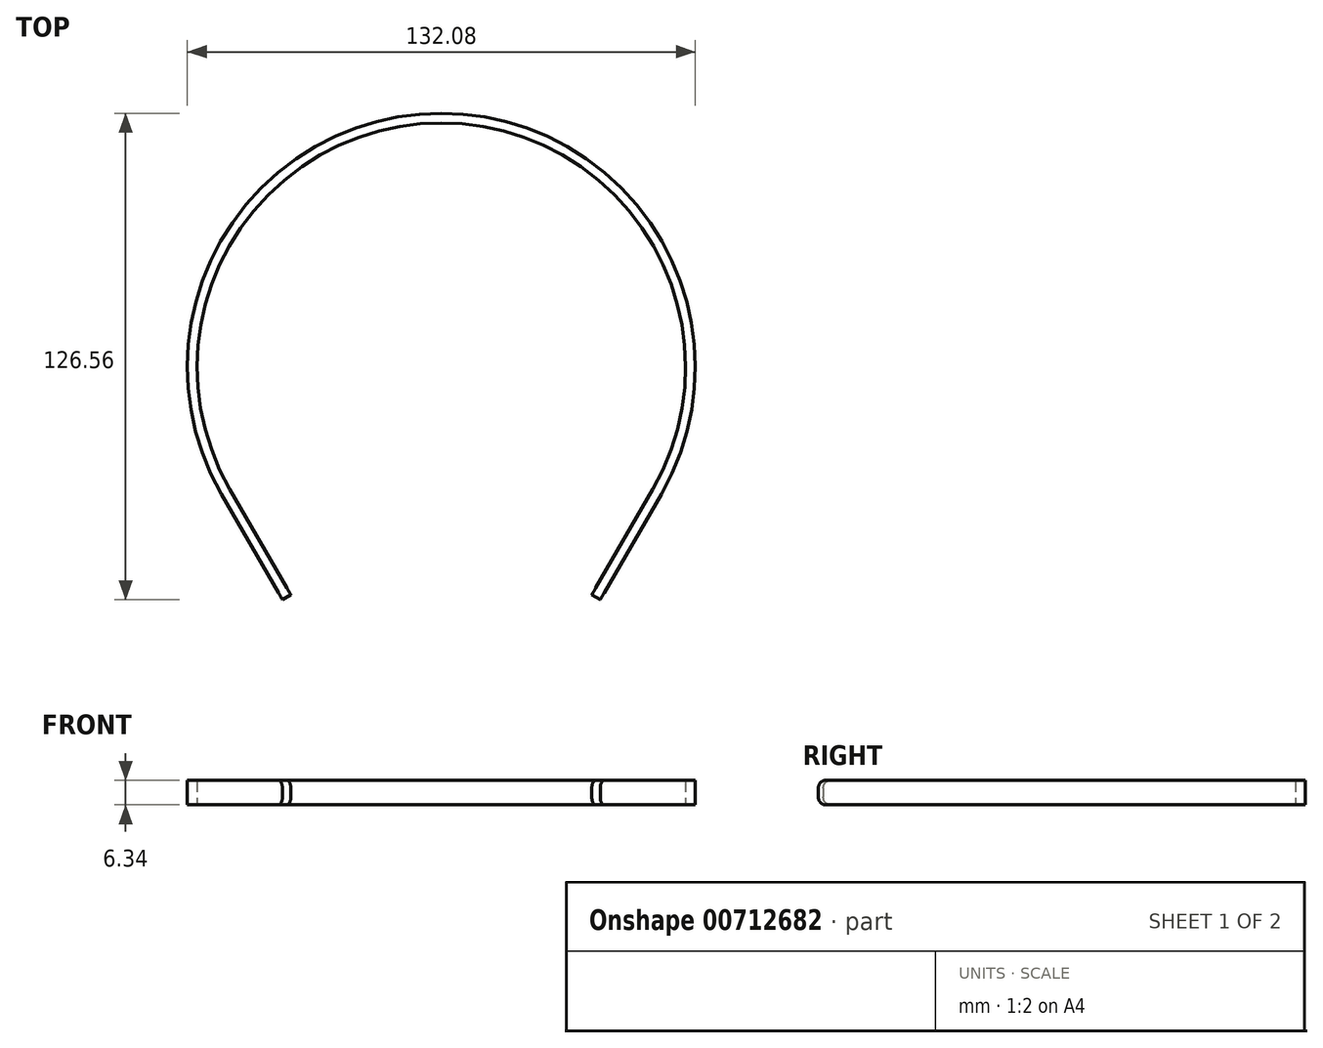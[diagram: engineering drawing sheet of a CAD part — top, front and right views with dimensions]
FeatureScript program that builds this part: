
annotation { "Feature Type Name" : "Feature", "Feature Type Description" : "" }
export const myFeature = defineFeature(function(context is Context, id is Id, definition is map)
    precondition{}
    {
        {
            var Q0;
            Q0=qCreatedBy(makeId("Top.planeOp"),FACE);
            var sketch = newSketch(context, id + "F0", { "sketchPlane" : qUnion([Q0])});
            skArc(sketch, "E0", {"start": v(57.2, -33.02) * mm, "mid": v(0, 66.04) * mm, "end": v(-57.2, -33.02) * mm});
            skArc(sketch, "E1", {"start": v(-55, -31.75) * mm, "mid": v(0, 63.5) * mm, "end": v(55, -31.75) * mm});
            skLineSegment(sketch, "E2", {"start": v(-57.2, -33.02) * mm, "end": v(0, 0) * mm, "construction": true});
            skLineSegment(sketch, "E3", {"start": v(0, 0) * mm, "end": v(57.2, -33.02) * mm, "construction": true});
            skLineSegment(sketch, "E4", {"start": v(-57.2, -33.02) * mm, "end": v(-41.32, -60.52) * mm});
            skLineSegment(sketch, "E5", {"start": v(-41.32, -60.52) * mm, "end": v(-39.12, -59.25) * mm});
            skLineSegment(sketch, "E6", {"start": v(-39.12, -59.25) * mm, "end": v(-55, -31.75) * mm});
            skLineSegment(sketch, "E7", {"start": v(55, -31.75) * mm, "end": v(39.12, -59.25) * mm});
            skLineSegment(sketch, "E8", {"start": v(39.12, -59.25) * mm, "end": v(41.32, -60.52) * mm});
            skLineSegment(sketch, "E9", {"start": v(41.32, -60.52) * mm, "end": v(57.2, -33.02) * mm});
            skSolve(sketch);
        }
        {
            var Q0;
            Q0=makeQuery(id+"F0.imprint","IMPRINT",FACE,{"disambiguationData":[TD([[makeQuery(id+"F0.imprint","IMPRINT",EDGE,{"derivedFrom":sQuery(id+"F0.wireOp",EDGE,"E0")}),1.0]])]});
            extrude(context, id + "F1", {"entities" : qUnion([Q0]), "endBound" : BoundingType.SYMMETRIC, "depth" : 6.35 * mm, "offsetDistance" : 25.4 * mm});
        }
        {
            var Q0;
            Q0=makeQuery(id+"F1.opExtrude","CAP_EDGE",EDGE,{"disambiguationData":[OSD([sQuery(id+"F0.wireOp",EDGE,"E8")])],"isStart":true});
            var Q1;
            Q1=makeQuery(id+"F1.opExtrude","CAP_EDGE",EDGE,{"disambiguationData":[OSD([sQuery(id+"F0.wireOp",EDGE,"E8")])],"isStart":false});
            var Q2;
            Q2=makeQuery(id+"F1.opExtrude","CAP_EDGE",EDGE,{"disambiguationData":[OSD([sQuery(id+"F0.wireOp",EDGE,"E5")])],"isStart":false});
            var Q3;
            Q3=makeQuery(id+"F1.opExtrude","CAP_EDGE",EDGE,{"disambiguationData":[OSD([sQuery(id+"F0.wireOp",EDGE,"E5")])],"isStart":true});
            fillet(context, id + "F2", {"entities" : qUnion([Q0, Q1, Q2, Q3]), "radius" : 2.03 * mm, "tangentPropagation" : true, "allowEdgeOverflow" : false});
        }
    });
